# Revit family: MT-PROVISTA _FSSF_GLZ
name_source: partatom
category: Windows
revit_build: Autodesk Revit 2017 (Build: 20160225_1515(x64)
units: mm (PartAtom-declared; Revit-internal decimal feet)

## family parameters
Always vertical = Yes
Cut with Voids When Loaded = No
Host = Wall
OmniClass Number = 23.30.20.00
OmniClass Title = Windows
Room Calculation Point = No
Shared = No

## types (1)
- FSSF
    ANZRC COMPLIANT = YES
    BOT PANEL POSITION = 52 mm  [stored 0.170604 ft]
    Default Sill Height = 900 mm  [stored 2.95276 ft]
    FRAME MATERIAL = <By Category>
    FRAME THICKNESS = 102 mm
    GLAZED MATERIAL = Glass
    Height = 2300 mm
    MAX HEIGHT = 2000 mm  [stored 6.56168 ft]
    MAX PANEL HEIGHT = 2000 mm  [stored 6.56168 ft]
    MAX PANEL WIDTH = 1500 mm  [stored 4.92126 ft]
    MAX WIDTH = 1500 mm  [stored 4.92126 ft]
    Manufacturer = ALSPEC
    Model = HAWKESBURY TOP HUNG COMMERCIAL SLIDING DOOR
    OFFSET = 10 mm  [stored 0.0328084 ft]
    OVERALL FRAME HEIGHT = 2000 mm  [stored 6.56168 ft]
    OVERALL FRAME WIDTH = 1200 mm
    PANEL HEIGHT = 549 mm
    PANEL WIDTH = 1067 mm
    Rough Height = 2000 mm  [stored 6.56168 ft]
    Rough Width = 1200 mm
    SINGLE GLAZED THICKNESS = 6 mm  [stored 0.019685 ft]
    TOLERANCE = 0 mm  [stored 0 ft]
    URL = WWW.ALSPEC.COM.AU
    VERSION = 2.1
    WARNING = No
    Wall Closure = By host
    Width = 1200 mm
    YEAR = 2019

note: [stored X ft] marks values corroborated as IEEE doubles in the binary element streams (Revit-internal decimal feet)

## geometry (parser evidence)
native form markers: Sweep x11
no freeform markers — native parametric forms only
